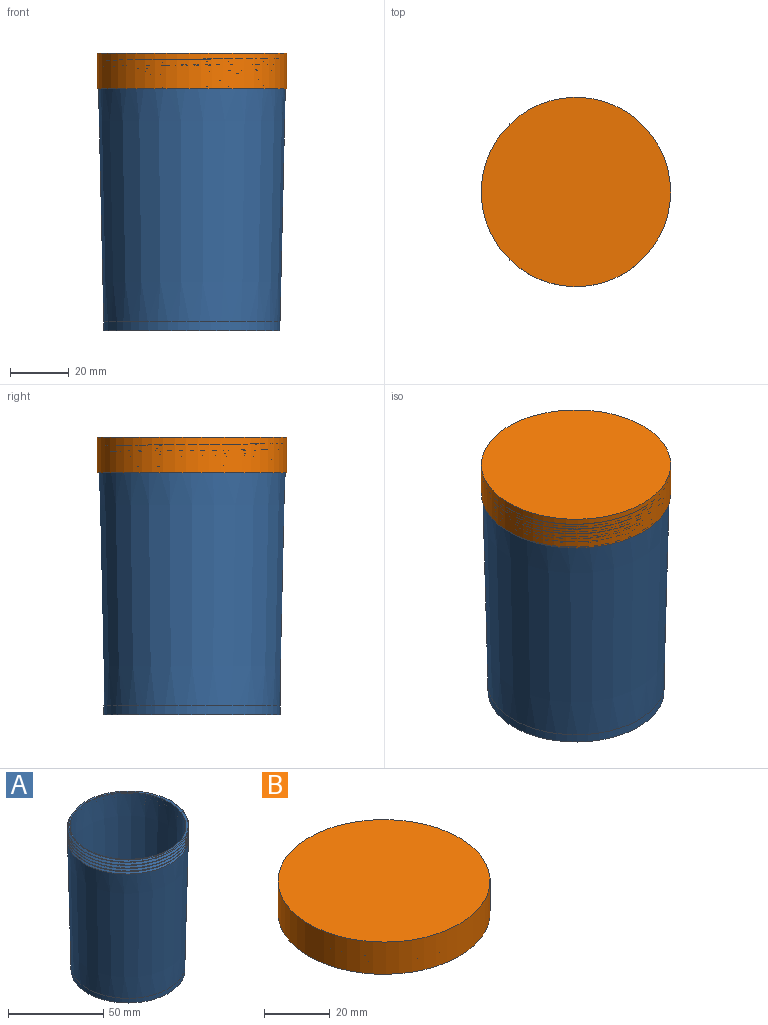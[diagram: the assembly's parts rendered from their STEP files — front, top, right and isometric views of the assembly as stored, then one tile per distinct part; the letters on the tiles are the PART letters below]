
ASSEMBLY  parts=2 mates=1
PART A: 20 faces, bbox 64.1x74x94.3 mm
  f0: cone r=30mm half-angle=1.3deg, axis (0,0,1), area 15774.5mm2, adj f1,f9,f17,f18,f19
  f1: cone r=30mm half-angle=1.3deg, axis (0,0,1), area 59mm2, adj f0,f2,f18,f19
  f2: cone r=30mm half-angle=1.3deg, axis (0,0,1), area 43.4mm2, adj f1,f3,f18,f19
  f3: cone r=30mm half-angle=1.3deg, axis (0,0,1), area 27.7mm2, adj f2,f4,f18,f19
  f4: cone r=30mm half-angle=1.3deg, axis (0,0,1), area 12mm2, adj f3,f5,f18,f19
  f5: cone r=30mm half-angle=1.3deg, axis (0,0,1), area 0mm2, adj f4,f6,f18
  f6: plane 62.96x62.95mm, normal (0,0,1), area 182.1mm2, adj f5,f7,f18,f19
  f7: cone r=28.5mm half-angle=1.3deg, axis (0,0,1), area 16429.1mm2, adj f6,f13
  f8: cylinder r=24mm len=48mm, axis (0,0,1), area 150.8mm2, adj f11,f16
  f9: cylinder r=30mm len=60mm, axis (0,0,1), area 565.5mm2, adj f0,f10
  f10: plane 60x60mm, normal (0,0,-1), area 703.7mm2, adj f9,f16
  f11: plane 48x48mm, normal (0,0,-1), area 1809.6mm2, adj f8
  f12: cylinder r=26mm len=52mm, axis (0,0,1), area 490.1mm2, adj f14,f15
  f13: cylinder r=28.53mm len=57.07mm, axis (0,0,1), area 537.8mm2, adj f7,f14
  f14: plane 57.07x57.07mm, normal (0,0,1), area 434.1mm2, adj f12,f13
  f15: plane 52x52mm, normal (0,0,1), area 2123.7mm2, adj f12
  f16: torus R=26mm, axis (0,0,-1), area 488.1mm2, adj f8,f10
  f17: plane 1.63x0.96mm, normal (-0.23,0.97,0), area 0.8mm2, adj f0,f18,f19
  f18: bspline ~74x64.08mm, area 1176.4mm2, adj f0,f1,f2,f3,f4,f5,f6,f17
  f19: bspline ~74x64.08mm, area 1278mm2, adj f0,f1,f2,f3,f4,f6,f17,f18
PART B: 8 faces, bbox 65.7x75x14.5 mm
  f0: cylinder r=30.75mm len=61.5mm, axis (0,0,1), area 303.5mm2, adj f2,f4,f5,f6,f7
  f1: cylinder r=32.25mm len=64.5mm, axis (0,0,1), area 2431.6mm2, adj f2,f3
  f2: plane 65.74x65.74mm, normal (0,0,-1), area 188.2mm2, adj f0,f1,f5,f6
  f3: plane 64.5x64.5mm, normal (0,0,1), area 3267.5mm2, adj f1
  f4: plane 61.5x61.5mm, normal (0,0,-1), area 2970.6mm2, adj f0
  f5: bspline ~73.74x63.86mm, area 1445.8mm2, adj f0,f2,f6,f7
  f6: bspline ~73.74x63.86mm, area 1304mm2, adj f0,f2,f5,f7
  f7: plane 1.98x1.18mm, normal (0,-1,0), area 1.2mm2, adj f0,f5,f6
PLACE A at identity
PLACE B t=(0,0,91.5)mm
MATE slider B.f0 <-> A.f0  axis (0,0,-1) through (0,0,90)mm
